# Revit family: Bjælke-IB
name_source: partatom
category: Structural Framing
units: mm (PartAtom-declared; Revit-internal decimal feet)

## family parameters
Always export as geometry = No
Always vertical = Yes
Cut with Voids When Loaded = No
Material for Model Behavior = Other
OmniClass Number = 23.25.30.11.14.14
OmniClass Title = Beams
Section Shape = Not Defined
Shared = No
Show family pre-cut in plan views = Yes
Structural Framing Length Roundoff = 0 mm

## types (4) — shared parameters
CRH_RFA_Bruger_LastRelease = kvn
CRH_RFA_Bruger_LastSave = kvn
CRH_RFA_TimeStamp_LastRelease = 20210825
CRH_RFA_TimeStamp_LastSave = 20210825
Chamfer Top = Yes
Manufacturer = CRH Concrete
Model = IB
Select Chamfer Top = Chamfer
Type Chamfer = Chamfer
Type Chamfer-None = Chamfer None

## per-type parameters (varying)
| type | Height | Width |
| IB30/60 | 600 mm  [stored 1.9685 ft] | 300 mm  [stored 0.984252 ft] |
| IB36/60 | 600 mm  [stored 1.9685 ft] | 360 mm  [stored 1.1811 ft] |
| IB42/96 | 960 mm  [stored 3.14961 ft] | 420 mm  [stored 1.37795 ft] |
| IB48/96 | 960 mm  [stored 3.14961 ft] | 480 mm  [stored 1.5748 ft] |

note: [stored X ft] marks values corroborated as IEEE doubles in the binary element streams (Revit-internal decimal feet)

## geometry (parser evidence)
native form markers: Blend x4, Sweep x12
no freeform markers — native parametric forms only
